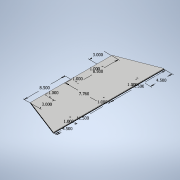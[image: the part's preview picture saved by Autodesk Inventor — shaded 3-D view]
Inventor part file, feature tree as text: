
AUTODESK INVENTOR PART (.ipt)
format: ipt  version: 2021 (Build 250183000, 183)  size: 119,296 bytes
history: native  units: in
note: dims shown in document units (in); Inventor stores cm internally (conversion verified against a paired STEP export)
features: sketch x1, extrude x1, hole x1
ambient origin geometry x8: Origin, YZ Plane, XZ Plane, XY Plane, X Axis, Y Axis, Z Axis, Center Point
bodies: Solid1 (feature_tree)
feature tree (3):
  sketch  "Sketch1"  dims[d0=11.5in d1=11.5in d2=7.76in d3=8.5in d4=8.5in d5=0.125in d6=0.0in d7=3.0in d8=1.0in d10=4.5in d11=4.5in d12=1.0in d13=1.0in d14=1.0in d15=1.0in d18=3.0in d19=1.0in d23=0.201in d24=0.75in d25=0.385in d26=0.25in d27=0.5635in d28=1.0in d29=0.8108in]
  extrude  "Extrusion1"  Depth=11.5in
  hole  "Hole1"  [1 undecoded]
note: 1 required parameter value undecoded (feature->parameter linkage not recoverable at this tier; creation-order binding heuristic only, values carry confidence <= 0.55)
